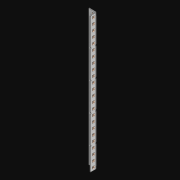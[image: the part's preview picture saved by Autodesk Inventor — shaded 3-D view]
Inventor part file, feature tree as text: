
AUTODESK INVENTOR PART (.ipt)
format: ipt  version: 2021 (Build 250183000, 183)  size: 1,251,328 bytes
history: native  units: in
note: dims shown in document units (in); Inventor stores cm internally (conversion verified against a paired STEP export)
features: extrude x50, other x48, sketch x4, pattern_linear x2, sheet_metal_op x1
ambient origin geometry x8: Origin, YZ Plane, XZ Plane, XY Plane, X Axis, Y Axis, Z Axis, Center Point
bodies: Solid1 (feature_tree)
feature tree (105):
  pattern_linear  "Rectangular Pattern1"  Spacing1=0.5in  [1 undecoded]
  pattern_linear  "Rectangular Pattern3"  Count1=24  [1 undecoded]
  extrude  "Extrusion1"  Depth=0.5in
  extrude  "Extrusion2"  Depth=0.5in
  sketch  "Sketch1"  dims[d0=0.182in]
  other  "Srf1"
  sketch  "Sketch3"  dims[d1=0.063in d2=0.0in]
  other  "Srf3"
  other  "Srf4"
  other  "Srf5"
  other  "Srf6"
  other  "Srf7"
  other  "Srf8"
  other  "Srf9"
  other  "Srf10"
  other  "Srf11"
  other  "Srf12"
  other  "Srf13"
  other  "Srf14"
  other  "Srf15"
  other  "Srf16"
  other  "Srf17"
  other  "Srf18"
  other  "Srf19"
  other  "Srf20"
  other  "Srf21"
  other  "Srf22"
  other  "Srf23"
  other  "Srf24"
  other  "Srf25"
  other  "Srf26"
  other  "Srf142"
  other  "Srf143"
  other  "Srf144"
  other  "Srf145"
  other  "Srf146"
  other  "Srf147"
  other  "Srf148"
  other  "Srf149"
  other  "Srf150"
  other  "Srf151"
  other  "Srf152"
  other  "Srf153"
  other  "Srf154"
  other  "Srf155"
  other  "Srf156"
  other  "Srf157"
  other  "Srf158"
  other  "Srf159"
  other  "Srf160"
  other  "Srf161"
  other  "Srf162"
  other  "Srf163"
  other  "Srf164"
  sketch  "Sketch4"  dims[d6=0.182in]
  sketch  "Sketch5"  dims[d7=0.063in d8=0.0in d11=0.5in d12=0.3937in d14=0.5in d18=9.4488in d20=0.5in d21=5.5in d22=0.0in d23=0.841in d24=0.0in]
  sheet_metal_op  "Fold1"
  extrude  "ExtrusionSrf1"  TaperAngle=0.0deg  [1 undecoded]
  extrude  "ExtrusionSrf3"  Depth=0.5in TaperAngle=0.0deg
  extrude  "ExtrusionSrf4"  [1 undecoded]
  extrude  "ExtrusionSrf5"  [1 undecoded]
  extrude  "ExtrusionSrf6"  [1 undecoded]
  extrude  "ExtrusionSrf7"  [1 undecoded]
  extrude  "ExtrusionSrf8"  [1 undecoded]
  extrude  "ExtrusionSrf9"  [1 undecoded]
  extrude  "ExtrusionSrf10"  [1 undecoded]
  extrude  "ExtrusionSrf11"  [1 undecoded]
  extrude  "ExtrusionSrf12"  [1 undecoded]
  extrude  "ExtrusionSrf13"  [1 undecoded]
  extrude  "ExtrusionSrf14"  [1 undecoded]
  extrude  "ExtrusionSrf15"  [1 undecoded]
  extrude  "ExtrusionSrf16"  [1 undecoded]
  extrude  "ExtrusionSrf17"  [1 undecoded]
  extrude  "ExtrusionSrf18"  [1 undecoded]
  extrude  "ExtrusionSrf19"  [1 undecoded]
  extrude  "ExtrusionSrf20"  [1 undecoded]
  extrude  "ExtrusionSrf21"  [1 undecoded]
  extrude  "ExtrusionSrf22"  [1 undecoded]
  extrude  "ExtrusionSrf23"  [1 undecoded]
  extrude  "ExtrusionSrf24"  [1 undecoded]
  extrude  "ExtrusionSrf25"  [1 undecoded]
  extrude  "ExtrusionSrf26"  [1 undecoded]
  extrude  "ExtrusionSrf142"  [1 undecoded]
  extrude  "ExtrusionSrf143"  [1 undecoded]
  extrude  "ExtrusionSrf144"  [1 undecoded]
  extrude  "ExtrusionSrf145"  [1 undecoded]
  extrude  "ExtrusionSrf146"  [1 undecoded]
  extrude  "ExtrusionSrf147"  [1 undecoded]
  extrude  "ExtrusionSrf148"  [1 undecoded]
  extrude  "ExtrusionSrf149"  [1 undecoded]
  extrude  "ExtrusionSrf150"  [1 undecoded]
  extrude  "ExtrusionSrf151"  [1 undecoded]
  extrude  "ExtrusionSrf152"  [1 undecoded]
  extrude  "ExtrusionSrf153"  [1 undecoded]
  extrude  "ExtrusionSrf154"  [1 undecoded]
  extrude  "ExtrusionSrf155"  [1 undecoded]
  extrude  "ExtrusionSrf156"  [1 undecoded]
  extrude  "ExtrusionSrf157"  [1 undecoded]
  extrude  "ExtrusionSrf158"  [1 undecoded]
  extrude  "ExtrusionSrf159"  [1 undecoded]
  extrude  "ExtrusionSrf160"  [1 undecoded]
  extrude  "ExtrusionSrf161"  [1 undecoded]
  extrude  "ExtrusionSrf162"  [1 undecoded]
  extrude  "ExtrusionSrf163"  [1 undecoded]
  extrude  "ExtrusionSrf164"  [1 undecoded]
note: 49 required parameter values undecoded (feature->parameter linkage not recoverable at this tier; creation-order binding heuristic only, values carry confidence <= 0.55)
